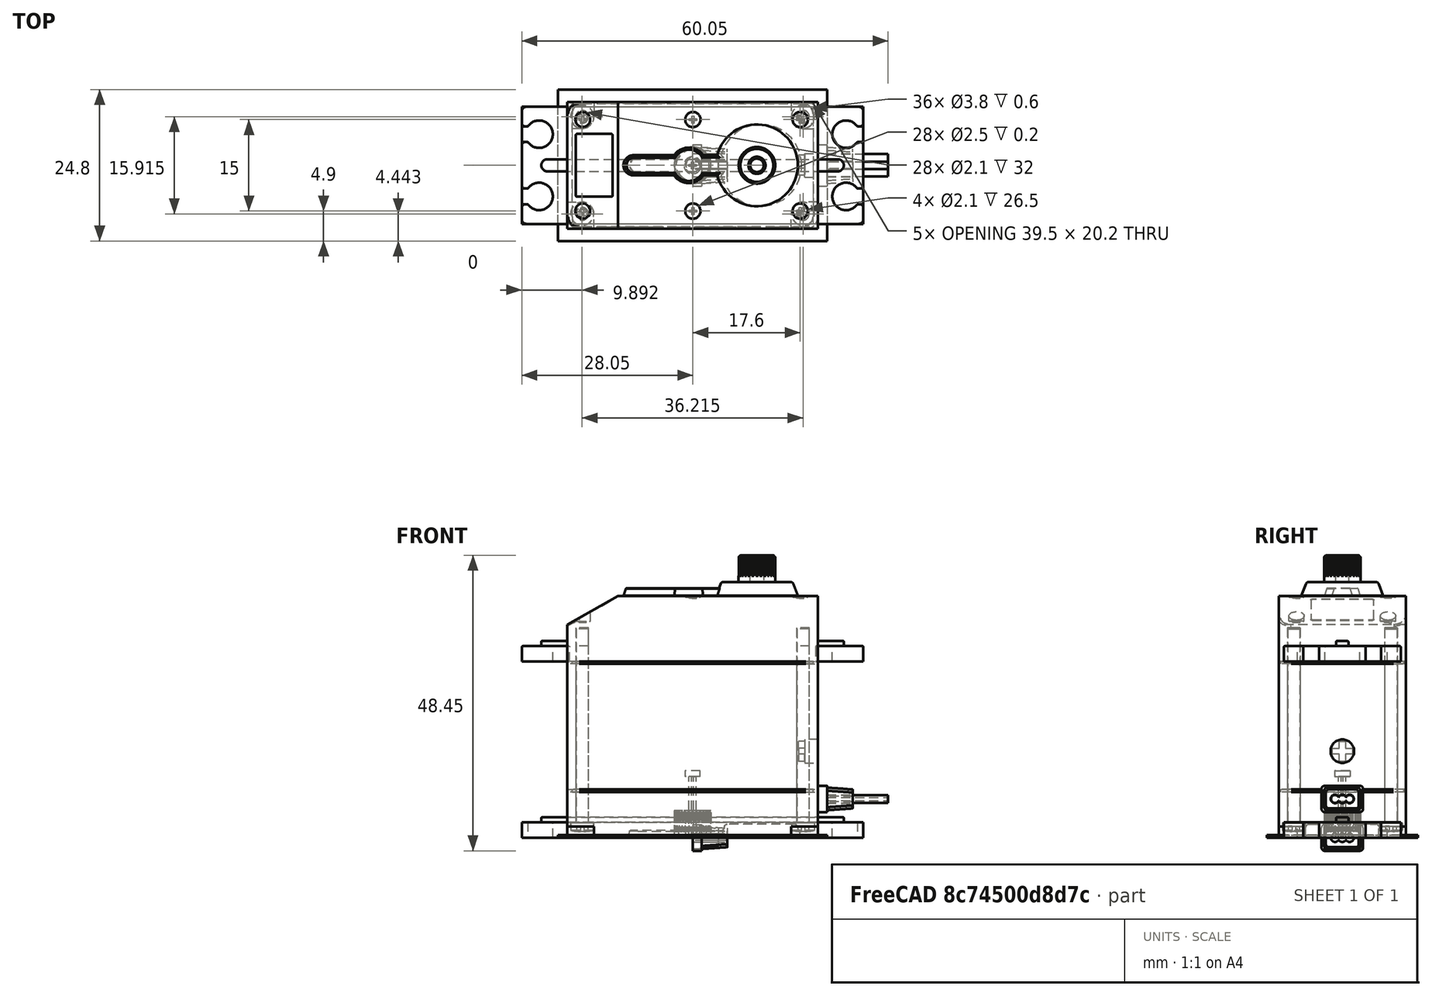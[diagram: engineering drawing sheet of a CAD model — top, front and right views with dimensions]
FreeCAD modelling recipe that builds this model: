
FCSTD DOCUMENT  (FreeCAD 0.19R24291 (Git))
Label: servo
License: CC-BY 3.0
LicenseURL: http://creativecommons.org/licenses/by/3.0/
objects: Sketcher::SketchObject×27, Part::Feature×24, PartDesign::Pocket×12, PartDesign::Pad×9, Part::Fillet×7, Part::MultiFuse×6, App::DocumentObjectGroup×5, Part::Compound×4, Part::Loft×3, PartDesign::Mirrored×2, Part::Cut×2, PartDesign::Fillet×2, PartDesign::Chamfer×2, PartDesign::PolarPattern×1, Part::Cylinder×1
note: 127 computed .brp shape members not serialized (recipe doc carries the construction recipe); baked Part::Feature solids carry a one-line shape summary decoded from their .brp

FEATURE [Sketcher::SketchObject] Sketch  label="servo-body-sketch"
  FullyConstrained = false
  MapMode = 5
  Placement = pos=(0,0,0) rot=(1,0,0;1.5708rad)
  sketch-geometry (5):
    g0: LineSegment StartX=20.55 StartY=39.6 StartZ=0 EndX=20.55 EndY=0 EndZ=0
    g1: LineSegment StartX=20.55 StartY=0 StartZ=0 EndX=-20.55 EndY=0 EndZ=0
    g2: LineSegment StartX=-20.55 StartY=0 StartZ=0 EndX=-20.55 EndY=34.9 EndZ=0
    g3: LineSegment StartX=-20.55 StartY=34.9 StartZ=0 EndX=-12.25 EndY=39.6 EndZ=0
    g4: LineSegment StartX=-12.25 StartY=39.6 StartZ=0 EndX=20.55 EndY=39.6 EndZ=0
  constraints (15):
    c: Coincident(g0,g1)
    c: Coincident(g1,g2)
    c: Horizontal(g1)
    c: Vertical(g0)
    c: Vertical(g2)
    c: Symmetric(g1,g0,g-2)
    c: PointOnObject(g1,g-1)
    c: DistanceX(g1) = -41.1
    c: DistanceY(g0) = -39.6
    c: Coincident(g3,g2)
    c: Horizontal(g4)
    c: Coincident(g4,g0)
    c: Coincident(g3,g4)
    c: DistanceY(g2) = 34.9
    c: DistanceX(g4) = 32.8
FEATURE [PartDesign::Pad] Pad  label="servo-body-1"
  AllowMultiFace = false
  Direction = (1,1,1)
  Length = 20.8
  Length2 = 100
  Midplane = true
  Placement = pos=(0,0,0) rot=(1,0,0;1.5708rad)
  Profile = -> Sketch
  Type = 0
FEATURE [Sketcher::SketchObject] Sketch001  label="bottom-master-sketch"
  ExternalGeometry = -> [Pad]
  FullyConstrained = false
  MapMode = 5
  Placement = pos=(0,0,0) rot=(1,0,0;3.14159rad)
  Support = -> [Pad]
  sketch-geometry (15):
    g0: LineSegment StartX=-20.55 StartY=10.4 StartZ=0 EndX=-18.2075 EndY=8.05754 EndZ=0
    g1: Circle CenterX=-18.2075 CenterY=8.05754 CenterZ=0 NormalX=0 NormalY=0 NormalZ=1 AngleXU=0 Radius=1.05
    g2: GeomPoint X=-18.95 Y=8.8 Z=0
    g3: LineSegment StartX=-18.2075 StartY=8.05754 StartZ=0 EndX=-18.2075 EndY=6 EndZ=0
    g4: LineSegment StartX=-18.2075 StartY=8.05754 StartZ=0 EndX=-16.15 EndY=8.05754 EndZ=0
    g5: LineSegment StartX=-20.55 StartY=6 StartZ=0 EndX=-20.55 EndY=10.4 EndZ=0
    g6: LineSegment StartX=-20.55 StartY=10.4 StartZ=0 EndX=-16.15 EndY=10.4 EndZ=0
    g7: LineSegment StartX=-16.15 StartY=10.4 StartZ=0 EndX=-16.15 EndY=8.05754 EndZ=0
    g8: ArcOfCircle CenterX=-18.2075 CenterY=8.05754 CenterZ=0 NormalX=0 NormalY=0 NormalZ=1 AngleXU=0 Radius=2.05754 StartAngle=4.71239 EndAngle=6.28319
    g9: LineSegment StartX=-20.55 StartY=6 StartZ=0 EndX=-18.2075 EndY=6 EndZ=0
    g10: ArcOfCircle CenterX=-18.2075 CenterY=-8.05754 CenterZ=0 NormalX=0 NormalY=0 NormalZ=1 AngleXU=0 Radius=2.05754 StartAngle=5.46325e-06 EndAngle=1.5708
    g11: LineSegment StartX=-18.2075 StartY=-6 StartZ=0 EndX=-20.55 EndY=-6 EndZ=0
    g12: LineSegment StartX=-20.55 StartY=-6 StartZ=0 EndX=-20.55 EndY=-10.4 EndZ=0
    g13: LineSegment StartX=-20.55 StartY=-10.4 StartZ=0 EndX=-16.15 EndY=-10.4 EndZ=0
    g14: LineSegment StartX=-16.15 StartY=-10.4 StartZ=0 EndX=-16.15 EndY=-8.05753 EndZ=0
  constraints (40):
    c: Coincident(g0,g-4)
    c: Angle(g-4,g0) = 0.785398
    c: Radius(g1) = 1.05
    c: Coincident(g1,g0)
    c: PointOnObject(g2,g0)
    c: PointOnObject(g2,g1)
    c: DistanceX(g2,g0) = -1.6
    c: Vertical(g3)
    c: Coincident(g3,g0)
    c: Coincident(g0,g4)
    c: Horizontal(g4)
    c: Equal(g3,g4)
    c: Coincident(g5,g6)
    c: Vertical(g5)
    c: Horizontal(g6)
    c: Vertical(g7)
    c: Coincident(g7,g6)
    c: Coincident(g7,g4)
    c: Coincident(g5,g0)
    c: Coincident(g8,g0)
    c: Coincident(g8,g4)
    c: Coincident(g3,g8)
    c: Coincident(g9,g5)
    c: Coincident(g9,g3)
    c: Horizontal(g9)
    c: DistanceY(g0,g5) = -4.4
    c: Horizontal(g11)
    c: Coincident(g11,g12)
    c: Vertical(g12)
    c: Coincident(g12,g13)
    c: Horizontal(g13)
    c: Coincident(g13,g14)
    c: Vertical(g14)
    c: Coincident(g12,g-4)
    c: Symmetric(g10,g0,g-1)
    c: Symmetric(g13,g6,g-1)
    c: Symmetric(g11,g3,g-1)
    c: Equal(g10,g8)
    c: Coincident(g10,g11)
    c: Coincident(g10,g14)
FEATURE [PartDesign::Pocket] Pocket  label="bottom-master"
  AllowMultiFace = false
  Length = 1.8
  Length2 = 100
  Placement = pos=(0,0,0) rot=(1,0,0;1.5708rad)
  Profile = -> Sketch001
  Type = 0
FEATURE [PartDesign::Mirrored] Mirrored  label="bottom-1"
  MirrorPlane = -> Sketch001 [V_Axis]
  Originals = -> [Pocket]
  Placement = pos=(0,0,0) rot=(1,0,0;1.5708rad)
FEATURE [Sketcher::SketchObject] Sketch002  label="bottom-2-sketch"
  ExternalGeometry = -> [Mirrored]
  FullyConstrained = false
  MapMode = 5
  Placement = pos=(0,1e-15,1.8) rot=(1,0,0;3.14159rad)
  Support = -> [Mirrored]
  sketch-geometry (10):
    g0: LineSegment StartX=-20.55 StartY=10.4 StartZ=0 EndX=-18.85 EndY=8.7 EndZ=0
    g1: Circle CenterX=-18.1075 CenterY=7.95754 CenterZ=0 NormalX=0 NormalY=0 NormalZ=1 AngleXU=0 Radius=1.05
    g2: Circle CenterX=-18.1075 CenterY=7.95754 CenterZ=0 NormalX=0 NormalY=0 NormalZ=1 AngleXU=0 Radius=1.9
    g3: Circle CenterX=-18.1075 CenterY=-7.95754 CenterZ=0 NormalX=0 NormalY=0 NormalZ=1 AngleXU=0 Radius=1.9
    g4: Circle CenterX=18.1075 CenterY=7.95754 CenterZ=0 NormalX=0 NormalY=0 NormalZ=1 AngleXU=0 Radius=1.9
    g5: Circle CenterX=18.1075 CenterY=-7.95754 CenterZ=0 NormalX=0 NormalY=0 NormalZ=1 AngleXU=0 Radius=1.9
    g6: LineSegment StartX=-18.1075 StartY=7.95754 StartZ=0 EndX=18.1075 EndY=7.95754 EndZ=0
    g7: LineSegment StartX=18.1075 StartY=7.95754 StartZ=0 EndX=18.1075 EndY=-7.95754 EndZ=0
    g8: LineSegment StartX=18.1075 StartY=-7.95754 StartZ=0 EndX=-18.1075 EndY=-7.95754 EndZ=0
    g9: LineSegment StartX=-18.1075 StartY=-7.95754 StartZ=0 EndX=-18.1075 EndY=7.95754 EndZ=0
  constraints (24):
    c: Angle(g0,g-3) = 0.785398
    c: Coincident(g0,g-3)
    c: Radius(g1) = 1.05
    c: PointOnObject(g1,g0)
    c: PointOnObject(g0,g1)
    c: DistanceX(g0,g0) = 1.7
    c: Coincident(g2,g1)
    c: Radius(g2) = 1.9
    c: Equal(g3,g2)
    c: Equal(g2,g4)
    c: Equal(g4,g5)
    c: Coincident(g6,g7)
    c: Coincident(g7,g8)
    c: Coincident(g8,g9)
    c: Coincident(g9,g6)
    c: Horizontal(g6)
    c: Horizontal(g8)
    c: Vertical(g7)
    c: Vertical(g9)
    c: Symmetric(g6,g7,g-1)
    c: Coincident(g6,g1)
    c: Coincident(g3,g8)
    c: Coincident(g6,g4)
    c: Coincident(g5,g7)
FEATURE [PartDesign::Pocket] Pocket001  label="bottom-2"
  AllowMultiFace = false
  Length = 0.6
  Length2 = 100
  Placement = pos=(0,0,0) rot=(1,0,0;1.5708rad)
  Profile = -> Sketch002
  Type = 0
FEATURE [Sketcher::SketchObject] Sketch003  label="bottom-drills-sketch"
  ExternalGeometry = -> [Pocket001]
  FullyConstrained = false
  MapMode = 5
  Placement = pos=(0,1.6e-15,2.4) rot=(1,0,0;3.14159rad)
  Support = -> [Pocket001]
  sketch-geometry (8):
    g0: Circle CenterX=-18.1075 CenterY=7.95754 CenterZ=0 NormalX=0 NormalY=0 NormalZ=1 AngleXU=0 Radius=1.05
    g1: LineSegment StartX=-18.1075 StartY=7.95754 StartZ=0 EndX=18.1075 EndY=7.95754 EndZ=0
    g2: LineSegment StartX=18.1075 StartY=7.95754 StartZ=0 EndX=18.1075 EndY=-7.95754 EndZ=0
    g3: LineSegment StartX=18.1075 StartY=-7.95754 StartZ=0 EndX=-18.1075 EndY=-7.95754 EndZ=0
    g4: LineSegment StartX=-18.1075 StartY=-7.95754 StartZ=0 EndX=-18.1075 EndY=7.95754 EndZ=0
    g5: Circle CenterX=-18.1075 CenterY=-7.95754 CenterZ=0 NormalX=0 NormalY=0 NormalZ=1 AngleXU=0 Radius=1.05
    g6: Circle CenterX=18.1075 CenterY=7.95754 CenterZ=0 NormalX=0 NormalY=0 NormalZ=1 AngleXU=0 Radius=1.05
    g7: Circle CenterX=18.1075 CenterY=-7.95754 CenterZ=0 NormalX=0 NormalY=0 NormalZ=1 AngleXU=0 Radius=1.05
  constraints (18):
    c: Coincident(g0,g-3)
    c: Radius(g0) = 1.05
    c: Coincident(g1,g2)
    c: Coincident(g2,g3)
    c: Coincident(g3,g4)
    c: Coincident(g4,g1)
    c: Horizontal(g1)
    c: Horizontal(g3)
    c: Vertical(g2)
    c: Vertical(g4)
    c: Symmetric(g1,g2,g-1)
    c: Coincident(g1,g0)
    c: Equal(g6,g5)
    c: Equal(g5,g7)
    c: Equal(g7,g0)
    c: Coincident(g3,g5)
    c: Coincident(g6,g1)
    c: Coincident(g7,g2)
FEATURE [PartDesign::Pocket] Pocket002  label="bottom-drills"
  AllowMultiFace = false
  Length = 32
  Length2 = 100
  Placement = pos=(0,0,0) rot=(1,0,0;1.5708rad)
  Profile = -> Sketch003
  Type = 0
FEATURE [Sketcher::SketchObject] Sketch004  label="top-drills-1-sketch"
  ExternalGeometry = -> [Pocket002]
  FullyConstrained = false
  MapMode = 5
  Placement = pos=(0,3.08e-14,39.6) rot=(0,0,1;3.14159rad)
  Support = -> [Pocket002]
  sketch-geometry (9):
    g0: LineSegment StartX=-17.65 StartY=7.5 StartZ=0 EndX=-0.05 EndY=7.5 EndZ=0
    g1: LineSegment StartX=-0.05 StartY=7.5 StartZ=0 EndX=-0.05 EndY=-7.5 EndZ=0
    g2: LineSegment StartX=-0.05 StartY=-7.5 StartZ=0 EndX=-17.65 EndY=-7.5 EndZ=0
    g3: LineSegment StartX=-17.65 StartY=-7.5 StartZ=0 EndX=-17.65 EndY=7.5 EndZ=0
    g4: Circle CenterX=-0.05 CenterY=-7.5 CenterZ=0 NormalX=0 NormalY=0 NormalZ=1 AngleXU=0 Radius=1.25
    g5: Circle CenterX=-17.65 CenterY=-7.5 CenterZ=0 NormalX=0 NormalY=0 NormalZ=1 AngleXU=0 Radius=1.25
    g6: Circle CenterX=-0.05 CenterY=7.5 CenterZ=0 NormalX=0 NormalY=0 NormalZ=1 AngleXU=0 Radius=1.25
    g7: Circle CenterX=-17.65 CenterY=7.5 CenterZ=0 NormalX=0 NormalY=0 NormalZ=1 AngleXU=0 Radius=1.25
    g8: LineSegment StartX=-20.55 StartY=-10.4 StartZ=0 EndX=-17.65 EndY=-7.5 EndZ=0
  constraints (22):
    c: Coincident(g0,g1)
    c: Coincident(g1,g2)
    c: Coincident(g2,g3)
    c: Coincident(g3,g0)
    c: Horizontal(g0)
    c: Horizontal(g2)
    c: Vertical(g1)
    c: Vertical(g3)
    c: Symmetric(g2,g0,g-1)
    c: Equal(g4,g7)
    c: Equal(g7,g6)
    c: Equal(g6,g5)
    c: Radius(g4) = 1.25
    c: Coincident(g4,g1)
    c: Coincident(g6,g0)
    c: Coincident(g5,g2)
    c: Coincident(g7,g0)
    c: DistanceY(g-1,g1) = -7.5
    c: DistanceX(g2) = -17.6
    c: Coincident(g8,g-3)
    c: Coincident(g8,g2)
    c: Angle(g-3,g8) = 0.785398
FEATURE [PartDesign::Pocket] Pocket003  label="top-drills-1"
  AllowMultiFace = false
  Length = 0.2
  Length2 = 100
  Placement = pos=(0,0,0) rot=(1,0,0;1.5708rad)
  Profile = -> Sketch004
  Type = 0
FEATURE [Sketcher::SketchObject] Sketch006  label="potentiometer-1-sketch"
  FullyConstrained = false
  MapMode = 5
  Placement = pos=(20.55,0,0) rot=(0.707107,0,0.707107;3.14159rad)
  Support = -> [Pocket003]
  sketch-geometry (2):
    g0: Circle CenterX=14.175 CenterY=0 CenterZ=0 NormalX=0 NormalY=0 NormalZ=1 AngleXU=0 Radius=1.925
    g1: GeomPoint X=16.1 Y=0 Z=0
  constraints (5):
    c: PointOnObject(g0,g-1)
    c: Radius(g0) = 1.925
    c: PointOnObject(g1,g-1)
    c: PointOnObject(g1,g0)
    c: DistanceX(g-1,g1) = 16.1
FEATURE [PartDesign::Pocket] Pocket004  label="potentiometer-hole"
  AllowMultiFace = false
  Length = 2.2
  Length2 = 100
  Placement = pos=(0,0,0) rot=(1,0,0;1.5708rad)
  Profile = -> Sketch006
  Type = 0
FEATURE [Sketcher::SketchObject] Sketch007  label="potentiometer-cross-sketch"
  ExternalGeometry = -> [Pocket004]
  FullyConstrained = false
  MapMode = 5
  Placement = pos=(18.35,0,0) rot=(0.707107,0,0.707107;3.14159rad)
  Support = -> [Pocket004]
  sketch-geometry (12):
    g0: LineSegment StartX=13.675 StartY=1.65 StartZ=0 EndX=14.675 EndY=1.65 EndZ=0
    g1: LineSegment StartX=14.675 StartY=1.65 StartZ=0 EndX=14.675 EndY=0.5 EndZ=0
    g2: LineSegment StartX=14.675 StartY=-1.65 StartZ=0 EndX=13.675 EndY=-1.65 EndZ=0
    g3: LineSegment StartX=13.675 StartY=-1.65 StartZ=0 EndX=13.675 EndY=-0.5 EndZ=0
    g4: LineSegment StartX=12.525 StartY=0.5 StartZ=0 EndX=13.675 EndY=0.5 EndZ=0
    g5: LineSegment StartX=15.825 StartY=0.5 StartZ=0 EndX=15.825 EndY=-0.5 EndZ=0
    g6: LineSegment StartX=15.825 StartY=-0.5 StartZ=0 EndX=14.675 EndY=-0.5 EndZ=0
    g7: LineSegment StartX=12.525 StartY=-0.5 StartZ=0 EndX=12.525 EndY=0.5 EndZ=0
    g8: LineSegment StartX=14.675 StartY=0.5 StartZ=0 EndX=15.825 EndY=0.5 EndZ=0
    g9: LineSegment StartX=13.675 StartY=-0.5 StartZ=0 EndX=12.525 EndY=-0.5 EndZ=0
    g10: LineSegment StartX=13.675 StartY=0.5 StartZ=0 EndX=13.675 EndY=1.65 EndZ=0
    g11: LineSegment StartX=14.675 StartY=-0.5 StartZ=0 EndX=14.675 EndY=-1.65 EndZ=0
  constraints (30):
    c: Coincident(g0,g1)
    c: Coincident(g11,g2)
    c: Coincident(g2,g3)
    c: Coincident(g10,g0)
    c: Horizontal(g0)
    c: Horizontal(g2)
    c: Vertical(g1)
    c: Vertical(g3)
    c: Coincident(g8,g5)
    c: Coincident(g5,g6)
    c: Coincident(g9,g7)
    c: Coincident(g7,g4)
    c: Horizontal(g4)
    c: Horizontal(g6)
    c: Vertical(g5)
    c: Vertical(g7)
    c: Symmetric(g4,g5,g-3)
    c: Symmetric(g0,g11,g-3)
    c: Tangent(g4,g8)
    c: Tangent(g6,g9)
    c: Coincident(g3,g9)
    c: Coincident(g10,g4)
    c: Tangent(g3,g10)
    c: Coincident(g1,g8)
    c: Coincident(g11,g6)
    c: Tangent(g1,g11)
    c: Equal(g4,g10)
    c: Equal(g7,g0)
    c: DistanceX(g5,g4) = -3.3
    c: DistanceY(g5) = -1
FEATURE [PartDesign::Pocket] Pocket005  label="potentiometer-cross"
  AllowMultiFace = false
  Length = 1
  Length2 = 100
  Placement = pos=(0,0,0) rot=(1,0,0;1.5708rad)
  Profile = -> Sketch007
  Type = 0
FEATURE [Sketcher::SketchObject] Sketch008  label="label-plate-sketch"
  ExternalGeometry = -> [Pocket005]
  FullyConstrained = false
  MapMode = 5
  Placement = pos=(-19.9538,7.43e-14,35.2376) rot=(-0.254782,0,0.966998;3.14159rad)
  Support = -> [Pocket005]
  sketch-geometry (8):
    g0: LineSegment StartX=-7.65321 StartY=5.15 StartZ=0 EndX=-1.15321 EndY=5.15 EndZ=0
    g1: LineSegment StartX=-0.953214 StartY=4.95 StartZ=0 EndX=-0.953214 EndY=-4.95 EndZ=0
    g2: LineSegment StartX=-1.15321 StartY=-5.15 StartZ=0 EndX=-7.65321 EndY=-5.15 EndZ=0
    g3: LineSegment StartX=-7.85321 StartY=-4.95 StartZ=0 EndX=-7.85321 EndY=4.95 EndZ=0
    g4: ArcOfCircle CenterX=-7.65321 CenterY=4.95 CenterZ=0 NormalX=0 NormalY=0 NormalZ=1 AngleXU=0 Radius=0.2 StartAngle=1.5708 EndAngle=3.14159
    g5: ArcOfCircle CenterX=-1.15321 CenterY=4.95 CenterZ=0 NormalX=0 NormalY=0 NormalZ=1 AngleXU=0 Radius=0.2 StartAngle=0 EndAngle=1.5708
    g6: ArcOfCircle CenterX=-1.15321 CenterY=-4.95 CenterZ=0 NormalX=0 NormalY=0 NormalZ=1 AngleXU=0 Radius=0.2 StartAngle=4.71239 EndAngle=6.28319
    g7: ArcOfCircle CenterX=-7.65321 CenterY=-4.95 CenterZ=0 NormalX=0 NormalY=0 NormalZ=1 AngleXU=0 Radius=0.2 StartAngle=3.14159 EndAngle=4.71239
  constraints (20):
    c: Horizontal(g0)
    c: Horizontal(g2)
    c: Vertical(g1)
    c: Vertical(g3)
    c: Tangent(g0,g4)
    c: Tangent(g3,g4)
    c: Tangent(g0,g5)
    c: Tangent(g1,g5)
    c: Tangent(g1,g6)
    c: Tangent(g2,g6)
    c: Tangent(g2,g7)
    c: Tangent(g3,g7)
    c: Equal(g4,g5)
    c: Equal(g5,g7)
    c: Equal(g7,g6)
    c: Symmetric(g5,g6,g-1)
    c: DistanceY(g0,g2) = -10.3
    c: DistanceX(g3,g1) = 6.9
    c: Radius(g4) = 0.2
    c: DistanceX(g3,g-3) = -1
FEATURE [PartDesign::Pocket] Pocket006  label="Label-plate"
  AllowMultiFace = false
  Length = 0.1
  Length2 = 100
  Placement = pos=(0,0,0) rot=(1,0,0;1.5708rad)
  Profile = -> Sketch008
  Type = 0
FEATURE [Sketcher::SketchObject] Sketch009  label="top-left-2-drills-sketch"
  FullyConstrained = false
  MapMode = 5
  Placement = pos=(0,1.011e-13,39.6) rot=(0,0,1;3.14159rad)
  Support = -> [Pocket006]
  sketch-geometry (4):
    g0: Circle CenterX=18 CenterY=7.5 CenterZ=0 NormalX=0 NormalY=0 NormalZ=1 AngleXU=0 Radius=1.25
    g1: Circle CenterX=18 CenterY=-7.5 CenterZ=0 NormalX=0 NormalY=0 NormalZ=1 AngleXU=0 Radius=1.25
    g2: LineSegment StartX=18 StartY=7.5 StartZ=0 EndX=18 EndY=0 EndZ=0
    g3: LineSegment StartX=18 StartY=7.5 StartZ=0 EndX=19.25 EndY=7.5 EndZ=0
  constraints (10):
    c: Radius(g0) = 1.25
    c: Equal(g1,g0)
    c: Symmetric(g0,g1,g-1)
    c: Coincident(g2,g0)
    c: Vertical(g2)
    c: PointOnObject(g2,g-1)
    c: DistanceY(g2) = -7.5
    c: Horizontal(g3)
    c: Coincident(g3,g0)
    c: PointOnObject(g3,g0)
FEATURE [PartDesign::Pocket] Pocket007  label="top-left-2-drills"
  AllowMultiFace = false
  Length = 4.1
  Length2 = 100
  Placement = pos=(0,0,0) rot=(1,0,0;1.5708rad)
  Profile = -> Sketch009
  Type = 0
FEATURE [Sketcher::SketchObject] Sketch010  label="top-drills-cross-1-sketch"
  FullyConstrained = false
  MapMode = 5
  sketch-geometry (13):
    g0: Circle CenterX=0 CenterY=0 CenterZ=0 NormalX=0 NormalY=0 NormalZ=1 AngleXU=0 Radius=1.25
    g1: LineSegment StartX=-0.15 StartY=0.6 StartZ=0 EndX=0.15 EndY=0.6 EndZ=0
    g2: LineSegment StartX=0.15 StartY=0.6 StartZ=0 EndX=0.15 EndY=0.15 EndZ=0
    g3: LineSegment StartX=0.15 StartY=-0.6 StartZ=0 EndX=-0.15 EndY=-0.6 EndZ=0
    g4: LineSegment StartX=-0.15 StartY=-0.6 StartZ=0 EndX=-0.15 EndY=-0.15 EndZ=0
    g5: LineSegment StartX=-0.6 StartY=0.15 StartZ=0 EndX=-0.15 EndY=0.15 EndZ=0
    g6: LineSegment StartX=0.6 StartY=0.15 StartZ=0 EndX=0.6 EndY=-0.15 EndZ=0
    g7: LineSegment StartX=0.6 StartY=-0.15 StartZ=0 EndX=0.15 EndY=-0.15 EndZ=0
    g8: LineSegment StartX=-0.6 StartY=-0.15 StartZ=0 EndX=-0.6 EndY=0.15 EndZ=0
    g9: LineSegment StartX=0.15 StartY=0.15 StartZ=0 EndX=0.6 EndY=0.15 EndZ=0
    g10: LineSegment StartX=-0.15 StartY=-0.15 StartZ=0 EndX=-0.6 EndY=-0.15 EndZ=0
    g11: LineSegment StartX=-0.15 StartY=0.15 StartZ=0 EndX=-0.15 EndY=0.6 EndZ=0
    g12: LineSegment StartX=0.15 StartY=-0.15 StartZ=0 EndX=0.15 EndY=-0.6 EndZ=0
  constraints (32):
    c: Coincident(g0,g-1)
    c: Radius(g0) = 1.25
    c: Coincident(g1,g2)
    c: Coincident(g12,g3)
    c: Coincident(g3,g4)
    c: Coincident(g11,g1)
    c: Horizontal(g1)
    c: Horizontal(g3)
    c: Vertical(g2)
    c: Vertical(g4)
    c: Symmetric(g1,g12,g-1)
    c: Coincident(g9,g6)
    c: Coincident(g6,g7)
    c: Coincident(g10,g8)
    c: Coincident(g8,g5)
    c: Horizontal(g5)
    c: Horizontal(g7)
    c: Vertical(g6)
    c: Vertical(g8)
    c: Symmetric(g5,g6,g-1)
    c: Tangent(g5,g9)
    c: Tangent(g7,g10)
    c: Coincident(g4,g10)
    c: Coincident(g11,g5)
    c: Tangent(g4,g11)
    c: Coincident(g2,g9)
    c: Coincident(g12,g7)
    c: Tangent(g2,g12)
    c: Equal(g5,g11)
    c: Equal(g8,g1)
    c: DistanceX(g5,g6) = 1.2
    c: DistanceX(g1) = 0.3
FEATURE [PartDesign::Pad] Pad001  label="top-drills-cross-1"
  AllowMultiFace = false
  Direction = (1,1,1)
  Length = 10
  Length2 = 100
  Profile = -> Sketch010
  Type = 0
FEATURE [Sketcher::SketchObject] Sketch011  label="top-drills-cross-2-sketch"
  FullyConstrained = false
  MapMode = 5
  Placement = pos=(0,0,10) rot=(0,0,1;0rad)
  Support = -> [Pad001]
  sketch-geometry (1):
    g0: Circle CenterX=0 CenterY=0 CenterZ=0 NormalX=0 NormalY=0 NormalZ=1 AngleXU=0 Radius=1.25
  constraints (2):
    c: Coincident(g0,g-1)
    c: Radius(g0) = 1.25
FEATURE [PartDesign::Pad] Pad002  label="top-drills-cross-2"
  AllowMultiFace = false
  Direction = (1,1,1)
  Length = 1
  Length2 = 100
  Profile = -> Sketch011
  Type = 0
FEATURE [Part::Feature] Pad002001  label="top-drills-cross-01"
  Placement = pos=(17.65,7.5,39.2) rot=(0,0,1;0rad)
  shape: bbox 2.5 x 2.5 x 11 mm, 16 faces (baked)
FEATURE [Part::Feature] Pad002001001  label="top-drills-cross-002"
  Placement = pos=(17.65,-7.5,39.2) rot=(0,0,1;0rad)
  shape: bbox 2.5 x 2.5 x 11 mm, 16 faces (baked)
FEATURE [Part::Feature] Pad002001002  label="top-drills-cross-003"
  Placement = pos=(0.05,7.5,39.2) rot=(0,0,1;0rad)
  shape: bbox 2.5 x 2.5 x 11 mm, 16 faces (baked)
FEATURE [Part::Feature] Pad002001003  label="top-drills-cross-004"
  Placement = pos=(0.05,-7.5,39.2) rot=(0,0,1;0rad)
  shape: bbox 2.5 x 2.5 x 11 mm, 16 faces (baked)
FEATURE [Part::Feature] Pad002001003001  label="top-drills-cross-005"
  Placement = pos=(-18,7.5,35.2) rot=(0,0,1;0rad)
  shape: bbox 2.5 x 2.5 x 11 mm, 16 faces (baked)
FEATURE [Part::Feature] Pad002001003002  label="top-drills-cross-006"
  Placement = pos=(-18,-7.5,35.2) rot=(0,0,1;0rad)
  shape: bbox 2.5 x 2.5 x 11 mm, 16 faces (baked)
FEATURE [Part::MultiFuse] Fusion  label="union-of-top-crosses"
  Shapes = -> [Pad002001,Pad002001003001,Pad002001003002,Pad002001002,Pad002001003,Pad002001001]
FEATURE [Part::Cut] Cut  label="servo-body-final-1"
  Base = -> Pocket007
  Tool = -> Fusion
FEATURE [Sketcher::SketchObject] Sketch012  label="shaft-anchor-sketch"
  ExternalGeometry = -> [Cut]
  FullyConstrained = false
  MapMode = 5
  Placement = pos=(0,1.187e-13,39.6) rot=(0,0,1;0rad)
  Support = -> [Cut]
  sketch-geometry (2):
    g0: Circle CenterX=10.55 CenterY=0 CenterZ=0 NormalX=0 NormalY=0 NormalZ=1 AngleXU=0 Radius=3
    g1: LineSegment StartX=13.55 StartY=0 StartZ=0 EndX=20.55 EndY=0 EndZ=0
  constraints (7):
    c: PointOnObject(g0,g-1)
    c: Radius(g0) = 3
    c: Horizontal(g1)
    c: PointOnObject(g1,g-3)
    c: PointOnObject(g1,g-1)
    c: PointOnObject(g1,g0)
    c: DistanceX(g1) = 7
FEATURE [PartDesign::Pad] Pad002001003003  label="servo-body-final-2"
  AllowMultiFace = false
  Direction = (1,1,1)
  Length = 0.1
  Length2 = 100
  Profile = -> Sketch012
  Type = 0
FEATURE [Sketcher::SketchObject] Sketch013  label="side-gap-sketch"
  FullyConstrained = false
  MapMode = 5
  sketch-geometry (25):
    g0: LineSegment StartX=-18.05 StartY=10.4 StartZ=0 EndX=18.05 EndY=10.4 EndZ=0
    g1: LineSegment StartX=20.05 StartY=8.4 StartZ=0 EndX=20.05 EndY=-8.4 EndZ=0
    g2: LineSegment StartX=18.05 StartY=-10.4 StartZ=0 EndX=-18.05 EndY=-10.4 EndZ=0
    g3: LineSegment StartX=-20.05 StartY=-8.4 StartZ=0 EndX=-20.05 EndY=8.4 EndZ=0
    g4: LineSegment StartX=-22.05 StartY=12.4 StartZ=0 EndX=-18.05 EndY=8.4 EndZ=0
    g5: LineSegment StartX=-18.05 StartY=10.1 StartZ=0 EndX=18.05 EndY=10.1 EndZ=0
    g6: LineSegment StartX=19.75 StartY=8.4 StartZ=0 EndX=19.75 EndY=-8.4 EndZ=0
    g7: LineSegment StartX=18.05 StartY=-10.1 StartZ=0 EndX=-18.05 EndY=-10.1 EndZ=0
    g8: LineSegment StartX=-19.75 StartY=-8.4 StartZ=0 EndX=-19.75 EndY=8.4 EndZ=0
    g9: LineSegment StartX=-22.05 StartY=12.4 StartZ=0 EndX=22.05 EndY=12.4 EndZ=0
    g10: LineSegment StartX=22.05 StartY=12.4 StartZ=0 EndX=22.05 EndY=-12.4 EndZ=0
    g11: LineSegment StartX=22.05 StartY=-12.4 StartZ=0 EndX=-22.05 EndY=-12.4 EndZ=0
    g12: LineSegment StartX=-22.05 StartY=-12.4 StartZ=0 EndX=-22.05 EndY=12.4 EndZ=0
    g13: ArcOfCircle CenterX=18.05 CenterY=-8.4 CenterZ=0 NormalX=0 NormalY=0 NormalZ=1 AngleXU=0 Radius=2 StartAngle=4.71239 EndAngle=6.28319
    g14: ArcOfCircle CenterX=18.05 CenterY=8.4 CenterZ=0 NormalX=0 NormalY=0 NormalZ=1 AngleXU=0 Radius=2 StartAngle=0 EndAngle=1.5708
    g15: ArcOfCircle CenterX=-18.05 CenterY=8.4 CenterZ=0 NormalX=0 NormalY=0 NormalZ=1 AngleXU=0 Radius=2 StartAngle=1.5708 EndAngle=3.14159
    g16: ArcOfCircle CenterX=-18.05 CenterY=-8.4 CenterZ=0 NormalX=0 NormalY=0 NormalZ=1 AngleXU=0 Radius=2 StartAngle=3.14159 EndAngle=4.71239
    g17: LineSegment StartX=-18.05 StartY=8.4 StartZ=0 EndX=18.05 EndY=8.4 EndZ=0
    g18: LineSegment StartX=18.05 StartY=8.4 StartZ=0 EndX=18.05 EndY=-8.4 EndZ=0
    g19: LineSegment StartX=18.05 StartY=-8.4 StartZ=0 EndX=-18.05 EndY=-8.4 EndZ=0
    g20: LineSegment StartX=-18.05 StartY=-8.4 StartZ=0 EndX=-18.05 EndY=8.4 EndZ=0
    g21: ArcOfCircle CenterX=-18.05 CenterY=8.4 CenterZ=0 NormalX=0 NormalY=0 NormalZ=1 AngleXU=0 Radius=1.7 StartAngle=1.5708 EndAngle=3.14159
    g22: ArcOfCircle CenterX=-18.05 CenterY=-8.4 CenterZ=0 NormalX=0 NormalY=0 NormalZ=1 AngleXU=0 Radius=1.7 StartAngle=3.14159 EndAngle=4.71239
    g23: ArcOfCircle CenterX=18.05 CenterY=-8.4 CenterZ=0 NormalX=0 NormalY=0 NormalZ=1 AngleXU=0 Radius=1.7 StartAngle=4.71239 EndAngle=6.28319
    g24: ArcOfCircle CenterX=18.05 CenterY=8.4 CenterZ=0 NormalX=0 NormalY=0 NormalZ=1 AngleXU=0 Radius=1.7 StartAngle=0 EndAngle=1.5708
  constraints (62):
    c: Horizontal(g0)
    c: Horizontal(g2)
    c: Vertical(g1)
    c: Vertical(g3)
    c: Angle(g-1,g4) = 2.35619
    c: Horizontal(g5)
    c: Horizontal(g7)
    c: Vertical(g6)
    c: Vertical(g8)
    c: Coincident(g9,g10)
    c: Coincident(g10,g11)
    c: Coincident(g11,g12)
    c: Coincident(g12,g9)
    c: Horizontal(g9)
    c: Horizontal(g11)
    c: Vertical(g10)
    c: Vertical(g12)
    c: PointOnObject(g9,g4)
    c: Symmetric(g9,g10,g-1)
    c: Coincident(g4,g9)
    c: Tangent(g1,g13)
    c: Tangent(g2,g13)
    c: Radius(g13) = 2
    c: Tangent(g0,g14)
    c: Tangent(g1,g14)
    c: Tangent(g0,g15)
    c: Tangent(g3,g15)
    c: Tangent(g2,g16)
    c: Tangent(g3,g16)
    c: Coincident(g17,g18)
    c: Coincident(g18,g19)
    c: Coincident(g19,g20)
    c: Coincident(g20,g17)
    c: Horizontal(g17)
    c: Horizontal(g19)
    c: Vertical(g18)
    c: Vertical(g20)
    c: Coincident(g17,g15)
    c: Symmetric(g15,g18,g-1)
    c: PointOnObject(g15,g4)
    c: Equal(g15,g16)
    c: Equal(g16,g14)
    c: Equal(g14,g13)
    c: DistanceX(g3,g1) = 40.1
    c: DistanceY(g0,g2) = -20.8
    c: Tangent(g8,g21)
    c: Tangent(g5,g21)
    c: PointOnObject(g21,g4)
    c: Coincident(g21,g15)
    c: Coincident(g4,g15)
    c: DistanceX(g8,g3) = -0.3
    c: DistanceX(g3,g4) = -2
    c: Tangent(g8,g22)
    c: Tangent(g7,g22)
    c: Coincident(g22,g16)
    c: Tangent(g7,g23)
    c: Tangent(g6,g23)
    c: Coincident(g23,g18)
    c: Tangent(g5,g24)
    c: Tangent(g6,g24)
    c: Coincident(g24,g17)
    c: Coincident(g14,g17)
FEATURE [PartDesign::Pad] Pad002001003004  label="side-gap-master"
  AllowMultiFace = false
  Direction = (1,1,1)
  Length = 0.4
  Length2 = 100
  Profile = -> Sketch013
  Type = 0
FEATURE [Sketcher::SketchObject] Sketch014  label="servo-top-1-sketch"
  FullyConstrained = false
  MapMode = 5
  sketch-geometry (10):
    g0: LineSegment StartX=-9.03485 StartY=1.65 StartZ=0 EndX=-9.03485 EndY=-1.65 EndZ=0
    g1: ArcOfCircle CenterX=-9.03485 CenterY=0 CenterZ=0 NormalX=0 NormalY=0 NormalZ=1 AngleXU=0 Radius=1.65 StartAngle=1.5708 EndAngle=4.71239
    g2: LineSegment StartX=-9.03485 StartY=1.65 StartZ=0 EndX=-2.38485 EndY=1.65 EndZ=0
    g3: LineSegment StartX=-9.03485 StartY=-1.65 StartZ=0 EndX=-2.38485 EndY=-1.65 EndZ=0
    g4: LineSegment StartX=11.1848 StartY=1.65 StartZ=0 EndX=11.1848 EndY=-1.65 EndZ=0
    g5: ArcOfCircle CenterX=0 CenterY=0 CenterZ=0 NormalX=0 NormalY=0 NormalZ=1 AngleXU=0 Radius=2.9 StartAngle=3.74684 EndAngle=5.67794
    g6: LineSegment StartX=2.38485 StartY=1.65 StartZ=0 EndX=11.1848 EndY=1.65 EndZ=0
    g7: ArcOfCircle CenterX=0 CenterY=0 CenterZ=0 NormalX=0 NormalY=0 NormalZ=1 AngleXU=0 Radius=2.9 StartAngle=0.605247 EndAngle=2.53635
    g8: LineSegment StartX=2.38485 StartY=-1.65 StartZ=0 EndX=11.1848 EndY=-1.65 EndZ=0
    g9: Circle CenterX=11.1848 CenterY=0 CenterZ=0 NormalX=0 NormalY=0 NormalZ=1 AngleXU=0 Radius=6.7
  constraints (29):
    c: Vertical(g0)
    c: Symmetric(g0,g0,g-1)
    c: Coincident(g1,g0)
    c: Coincident(g0,g1)
    c: PointOnObject(g1,g0)
    c: Horizontal(g2)
    c: Coincident(g2,g0)
    c: Horizontal(g3)
    c: Coincident(g3,g0)
    c: Coincident(g6,g4)
    c: Vertical(g4)
    c: Coincident(g4,g8)
    c: Tangent(g2,g6)
    c: PointOnObject(g7,g2)
    c: Equal(g5,g7)
    c: Coincident(g7,g6)
    c: Coincident(g5,g7)
    c: Coincident(g3,g5)
    c: Coincident(g8,g5)
    c: Tangent(g3,g8)
    c: Coincident(g7,g2)
    c: Coincident(g5,g-1)
    c: DistanceY(g0) = -3.3
    c: DistanceX(g0,g2) = 6.65
    c: Radius(g7) = 2.9
    c: Radius(g9) = 6.7
    c: PointOnObject(g9,g-1)
    c: PointOnObject(g9,g4)
    c: DistanceX(g6,g9) = 8.8
FEATURE [Sketcher::SketchObject] Sketch015  label="servo-top-1-sketch2"
  FullyConstrained = false
  MapMode = 5
  Placement = pos=(0,0,1.16) rot=(0,0,1;0rad)
  sketch-geometry (10):
    g0: LineSegment StartX=-8.99374 StartY=1.3 StartZ=0 EndX=-8.99374 EndY=-1.3 EndZ=0
    g1: ArcOfCircle CenterX=-8.99374 CenterY=0 CenterZ=0 NormalX=0 NormalY=0 NormalZ=1 AngleXU=0 Radius=1.3 StartAngle=1.5708 EndAngle=4.71239
    g2: LineSegment StartX=-8.99374 StartY=1.3 StartZ=0 EndX=-2.19374 EndY=1.3 EndZ=0
    g3: LineSegment StartX=-8.99374 StartY=-1.3 StartZ=0 EndX=-2.19374 EndY=-1.3 EndZ=0
    g4: LineSegment StartX=11.1937 StartY=1.3 StartZ=0 EndX=11.1937 EndY=-1.3 EndZ=0
    g5: ArcOfCircle CenterX=0 CenterY=0 CenterZ=0 NormalX=0 NormalY=0 NormalZ=1 AngleXU=0 Radius=2.55 StartAngle=3.67655 EndAngle=5.74823
    g6: LineSegment StartX=2.19374 StartY=1.3 StartZ=0 EndX=11.1937 EndY=1.3 EndZ=0
    g7: ArcOfCircle CenterX=0 CenterY=0 CenterZ=0 NormalX=0 NormalY=0 NormalZ=1 AngleXU=0 Radius=2.55 StartAngle=0.534957 EndAngle=2.60664
    g8: LineSegment StartX=2.19374 StartY=-1.3 StartZ=0 EndX=11.1937 EndY=-1.3 EndZ=0
    g9: Circle CenterX=11.1937 CenterY=0 CenterZ=0 NormalX=0 NormalY=0 NormalZ=1 AngleXU=0 Radius=6.7
  constraints (29):
    c: Vertical(g0)
    c: Symmetric(g0,g0,g-1)
    c: Coincident(g1,g0)
    c: Coincident(g0,g1)
    c: PointOnObject(g1,g0)
    c: Horizontal(g2)
    c: Coincident(g2,g0)
    c: Horizontal(g3)
    c: Coincident(g3,g0)
    c: Coincident(g6,g4)
    c: Vertical(g4)
    c: Coincident(g4,g8)
    c: Tangent(g2,g6)
    c: PointOnObject(g7,g2)
    c: Equal(g5,g7)
    c: Coincident(g7,g6)
    c: Coincident(g5,g7)
    c: Coincident(g3,g5)
    c: Coincident(g8,g5)
    c: Tangent(g3,g8)
    c: Coincident(g7,g2)
    c: Coincident(g5,g-1)
    c: DistanceY(g0) = -2.6
    c: DistanceX(g0,g2) = 6.8
    c: Radius(g7) = 2.55
    c: Radius(g9) = 6.7
    c: PointOnObject(g9,g-1)
    c: PointOnObject(g9,g4)
    c: DistanceX(g6,g9) = 9
FEATURE [Part::Loft] Loft  label="servo-top-1"
  Closed = false
  MaxDegree = 5
  Ruled = false
  Sections = -> [Sketch014,Sketch015]
  Solid = true
FEATURE [Sketcher::SketchObject] Sketch016  label="shaft-base-1-sketch"
  FullyConstrained = false
  MapMode = 5
  sketch-geometry (1):
    g0: Circle CenterX=0 CenterY=0 CenterZ=0 NormalX=0 NormalY=0 NormalZ=1 AngleXU=0 Radius=6.7
  constraints (2):
    c: Radius(g0) = 6.7
    c: Coincident(g-1,g0)
FEATURE [Sketcher::SketchObject] Sketch017  label="shaft-base-1-sketch2"
  FullyConstrained = false
  MapMode = 5
  Placement = pos=(0,0,2.2) rot=(0,0,1;0rad)
  sketch-geometry (1):
    g0: Circle CenterX=0 CenterY=0 CenterZ=0 NormalX=0 NormalY=0 NormalZ=1 AngleXU=0 Radius=5.85
  constraints (2):
    c: Radius(g0) = 5.85
    c: Coincident(g-1,g0)
FEATURE [Part::Loft] Loft001  label="Shaft-base-1"
  Closed = false
  MaxDegree = 5
  Placement = pos=(11.1848,0,0) rot=(0,0,1;0rad)
  Ruled = false
  Sections = -> [Sketch016,Sketch017]
  Solid = true
FEATURE [Part::MultiFuse] Fusion002  label="top-part-1"
  Shapes = -> [Loft,Loft001]
FEATURE [PartDesign::Fillet] Fillet
  Base = -> Fusion002 [Edge25]
  Radius = 0.5
  SupportTransform = false
FEATURE [Part::Fillet] Fillet001  label="top-part-2"
  Base = -> Fillet
  Edges = 8 edges r=0.1: [Edge6,Edge17,Edge19,Edge20,Edge21,Edge22,Edge23,Edge24]
FEATURE [App::DocumentObjectGroup] Group001  label="top-part-src"
  Group = -> [Fusion002,Fillet001]
FEATURE [Part::Feature] Fillet002  label="top-part"
  Placement = pos=(-0.634848,0,39.7) rot=(0,0,1;0rad)
  shape: bbox 28.82 x 13.4 x 14.16 mm, 24 faces (baked)
FEATURE [Sketcher::SketchObject] Sketch019  label="ears-body-1-sketch"
  FullyConstrained = false
  MapMode = 5
  sketch-geometry (4):
    g0: LineSegment StartX=-28 StartY=9.6 StartZ=0 EndX=28 EndY=9.6 EndZ=0
    g1: LineSegment StartX=28 StartY=9.6 StartZ=0 EndX=28 EndY=-9.6 EndZ=0
    g2: LineSegment StartX=28 StartY=-9.6 StartZ=0 EndX=-28 EndY=-9.6 EndZ=0
    g3: LineSegment StartX=-28 StartY=-9.6 StartZ=0 EndX=-28 EndY=9.6 EndZ=0
  constraints (11):
    c: Coincident(g0,g1)
    c: Coincident(g1,g2)
    c: Coincident(g2,g3)
    c: Coincident(g3,g0)
    c: Horizontal(g0)
    c: Horizontal(g2)
    c: Vertical(g1)
    c: Vertical(g3)
    c: Symmetric(g0,g1,g-1)
    c: DistanceX(g0) = 56
    c: DistanceY(g3) = 19.2
FEATURE [PartDesign::Pad] Pad002001003004001002  label="ears-body-1"
  AllowMultiFace = false
  Direction = (1,1,1)
  Length = 2.5
  Length2 = 100
  Profile = -> Sketch019
  Type = 0
FEATURE [Sketcher::SketchObject] Sketch020  label="right-ears-sketch"
  FullyConstrained = false
  MapMode = 5
  Placement = pos=(0,0,2.5) rot=(0,0,1;0rad)
  Support = -> [Pad002001003004001002]
  sketch-geometry (9):
    g0: ArcOfCircle CenterX=25.15 CenterY=5.1 CenterZ=0 NormalX=0 NormalY=0 NormalZ=1 AngleXU=0 Radius=2.25 StartAngle=0.605154 EndAngle=5.67803
    g1: LineSegment StartX=22.9 StartY=5.1 StartZ=0 EndX=25.15 EndY=5.1 EndZ=0
    g2: LineSegment StartX=27.0004 StartY=6.38 StartZ=0 EndX=29.0004 EndY=6.38 EndZ=0
    g3: LineSegment StartX=29.0004 StartY=6.38 StartZ=0 EndX=29.0004 EndY=3.82 EndZ=0
    g4: LineSegment StartX=29.0004 StartY=3.82 StartZ=0 EndX=27.0004 EndY=3.82 EndZ=0
    g5: ArcOfCircle CenterX=25.15 CenterY=-5.1 CenterZ=0 NormalX=0 NormalY=0 NormalZ=1 AngleXU=0 Radius=2.25 StartAngle=0.605154 EndAngle=5.67803
    g6: LineSegment StartX=27.0004 StartY=-3.82 StartZ=0 EndX=29.0004 EndY=-3.82 EndZ=0
    g7: LineSegment StartX=29.0004 StartY=-3.82 StartZ=0 EndX=29.0004 EndY=-6.38 EndZ=0
    g8: LineSegment StartX=29.0004 StartY=-6.38 StartZ=0 EndX=27.0004 EndY=-6.38 EndZ=0
  constraints (28):
    c: Radius(g0) = 2.25
    c: DistanceX(g0) = 25.15
    c: DistanceY(g0) = 5.1
    c: Horizontal(g1)
    c: PointOnObject(g1,g0)
    c: Coincident(g1,g0)
    c: Coincident(g2,g3)
    c: Coincident(g3,g4)
    c: Horizontal(g2)
    c: Horizontal(g4)
    c: Vertical(g3)
    c: Coincident(g0,g2)
    c: Coincident(g0,g4)
    c: Symmetric(g0,g0,g1)
    c: DistanceY(g3) = -2.56
    c: DistanceX(g2) = 2
    c: Symmetric(g5,g0,g-1)
    c: Equal(g0,g5)
    c: Coincident(g6,g7)
    c: Coincident(g7,g8)
    c: Horizontal(g6)
    c: Horizontal(g8)
    c: Vertical(g7)
    c: Coincident(g6,g5)
    c: Coincident(g8,g5)
    c: Symmetric(g5,g0,g-1)
    c: Symmetric(g0,g5,g-1)
    c: Symmetric(g6,g3,g-1)
FEATURE [PartDesign::Pocket] Pocket008  label="right-ear"
  AllowMultiFace = false
  Length = 5
  Length2 = 100
  Profile = -> Sketch020
  Type = 1
FEATURE [PartDesign::Mirrored] Mirrored001  label="ears-block-1"
  MirrorPlane = -> Sketch020 [V_Axis]
  Originals = -> [Pocket008]
FEATURE [Sketcher::SketchObject] Sketch021  label="ears-block-2-sketch"
  FullyConstrained = false
  MapMode = 5
  Placement = pos=(0,0,2.5) rot=(0,0,1;0rad)
  Support = -> [Mirrored001]
  sketch-geometry (6):
    g0: ArcOfCircle CenterX=-23.8 CenterY=0 CenterZ=0 NormalX=0 NormalY=0 NormalZ=1 AngleXU=0 Radius=1 StartAngle=1.57079 EndAngle=4.7124
    g1: ArcOfCircle CenterX=23.8 CenterY=0 CenterZ=0 NormalX=0 NormalY=0 NormalZ=1 AngleXU=0 Radius=1 StartAngle=4.71238 EndAngle=7.85399
    g2: LineSegment StartX=-23.8 StartY=-1 StartZ=0 EndX=23.8 EndY=-1 EndZ=0
    g3: LineSegment StartX=-23.8 StartY=1 StartZ=0 EndX=23.8 EndY=1 EndZ=0
    g4: GeomPoint X=-24.8 Y=0 Z=0
    g5: GeomPoint X=24.8 Y=0 Z=0
  constraints (18):
    c: Tangent(g0,g2)
    c: Tangent(g0,g3)
    c: Tangent(g1,g2)
    c: Tangent(g1,g3)
    c: Coincident(g0,g3)
    c: Coincident(g0,g2)
    c: Coincident(g2,g1)
    c: Coincident(g3,g1)
    c: Horizontal(g2)
    c: Equal(g0,g1)
    c: Symmetric(g0,g1,g-2)
    c: PointOnObject(g0,g-1)
    c: DistanceY(g0,g0) = 2
    c: PointOnObject(g4,g-1)
    c: PointOnObject(g4,g0)
    c: PointOnObject(g5,g-1)
    c: PointOnObject(g5,g1)
    c: DistanceX(g4,g5) = 49.6
FEATURE [PartDesign::Pad] Pad002001003004001003  label="ears-block-2"
  AllowMultiFace = false
  Direction = (1,1,1)
  Length = 0.86
  Length2 = 100
  Profile = -> Sketch021
  Type = 0
FEATURE [Sketcher::SketchObject] Sketch022  label="wire-holder-base-sketch"
  FullyConstrained = false
  MapMode = 5
  Placement = pos=(0,0,0) rot=(0.57735,0.57735,0.57735;2.0944rad)
  sketch-geometry (4):
    g0: LineSegment StartX=-3.4 StartY=2.15 StartZ=0 EndX=3.4 EndY=2.15 EndZ=0
    g1: LineSegment StartX=3.4 StartY=2.15 StartZ=0 EndX=3.4 EndY=-2.15 EndZ=0
    g2: LineSegment StartX=3.4 StartY=-2.15 StartZ=0 EndX=-3.4 EndY=-2.15 EndZ=0
    g3: LineSegment StartX=-3.4 StartY=-2.15 StartZ=0 EndX=-3.4 EndY=2.15 EndZ=0
  constraints (11):
    c: Coincident(g0,g1)
    c: Coincident(g1,g2)
    c: Coincident(g2,g3)
    c: Coincident(g3,g0)
    c: Horizontal(g0)
    c: Horizontal(g2)
    c: Vertical(g1)
    c: Vertical(g3)
    c: Symmetric(g0,g1,g-1)
    c: DistanceY(g1) = -4.3
    c: DistanceX(g0) = 6.8
FEATURE [PartDesign::Pad] Pad002001003004001005  label="wire-holder-base"
  AllowMultiFace = false
  Direction = (1,1,1)
  Length = 1.5
  Length2 = 100
  Placement = pos=(0,0,0) rot=(0.57735,0.57735,0.57735;2.0944rad)
  Profile = -> Sketch022
  Type = 0
FEATURE [Sketcher::SketchObject] Sketch023  label="wire-holder-body-1-sketch"
  FullyConstrained = false
  MapMode = 5
  Placement = pos=(0,0,0) rot=(0.57735,0.57735,0.57735;2.0944rad)
  sketch-geometry (4):
    g0: LineSegment StartX=-2.975 StartY=1.85 StartZ=0 EndX=2.975 EndY=1.85 EndZ=0
    g1: LineSegment StartX=2.975 StartY=1.85 StartZ=0 EndX=2.975 EndY=-1.85 EndZ=0
    g2: LineSegment StartX=2.975 StartY=-1.85 StartZ=0 EndX=-2.975 EndY=-1.85 EndZ=0
    g3: LineSegment StartX=-2.975 StartY=-1.85 StartZ=0 EndX=-2.975 EndY=1.85 EndZ=0
  constraints (11):
    c: Coincident(g0,g1)
    c: Coincident(g1,g2)
    c: Coincident(g2,g3)
    c: Coincident(g3,g0)
    c: Horizontal(g0)
    c: Horizontal(g2)
    c: Vertical(g1)
    c: Vertical(g3)
    c: Symmetric(g0,g1,g-1)
    c: DistanceX(g0) = 5.95
    c: DistanceY(g3) = 3.7
FEATURE [Sketcher::SketchObject] Sketch024  label="wire-holder-body-1-sketch2"
  FullyConstrained = false
  MapMode = 5
  Placement = pos=(4.2,0,0) rot=(0.57735,0.57735,0.57735;2.0944rad)
  sketch-geometry (4):
    g0: LineSegment StartX=-2.7 StartY=1.55 StartZ=0 EndX=2.7 EndY=1.55 EndZ=0
    g1: LineSegment StartX=2.7 StartY=1.55 StartZ=0 EndX=2.7 EndY=-1.55 EndZ=0
    g2: LineSegment StartX=2.7 StartY=-1.55 StartZ=0 EndX=-2.7 EndY=-1.55 EndZ=0
    g3: LineSegment StartX=-2.7 StartY=-1.55 StartZ=0 EndX=-2.7 EndY=1.55 EndZ=0
  constraints (11):
    c: Coincident(g0,g1)
    c: Coincident(g1,g2)
    c: Coincident(g2,g3)
    c: Coincident(g3,g0)
    c: Horizontal(g0)
    c: Horizontal(g2)
    c: Vertical(g1)
    c: Vertical(g3)
    c: Symmetric(g0,g1,g-1)
    c: DistanceX(g0) = 5.4
    c: DistanceY(g1) = -3.1
FEATURE [Part::Loft] Loft002  label="wire-holder-body-1"
  Closed = false
  MaxDegree = 5
  Ruled = false
  Sections = -> [Sketch023,Sketch024]
  Solid = true
FEATURE [Sketcher::SketchObject] Sketch025  label="wire-holes-sketch"
  FullyConstrained = false
  MapMode = 5
  Placement = pos=(4.2,-7e-16,0) rot=(0.57735,0.57735,0.57735;2.0944rad)
  Support = -> [Loft002]
  sketch-geometry (8):
    g0: ArcOfCircle CenterX=-1.2 CenterY=0 CenterZ=0 NormalX=0 NormalY=0 NormalZ=1 AngleXU=0 Radius=0.7 StartAngle=0.666946 EndAngle=5.61624
    g1: LineSegment StartX=-0.65 StartY=0.433013 StartZ=0 EndX=-0.55 EndY=0.433013 EndZ=0
    g2: ArcOfCircle CenterX=0 CenterY=0 CenterZ=0 NormalX=0 NormalY=0 NormalZ=1 AngleXU=0 Radius=0.7 StartAngle=0.666946 EndAngle=2.47465
    g3: LineSegment StartX=0.55 StartY=0.433013 StartZ=0 EndX=0.65 EndY=0.433013 EndZ=0
    g4: LineSegment StartX=-0.65 StartY=-0.433013 StartZ=0 EndX=-0.55 EndY=-0.433013 EndZ=0
    g5: ArcOfCircle CenterX=0 CenterY=0 CenterZ=0 NormalX=0 NormalY=0 NormalZ=1 AngleXU=0 Radius=0.7 StartAngle=3.80854 EndAngle=5.61624
    g6: ArcOfCircle CenterX=1.2 CenterY=0 CenterZ=0 NormalX=0 NormalY=0 NormalZ=1 AngleXU=0 Radius=0.7 StartAngle=3.80854 EndAngle=8.75783
    g7: LineSegment StartX=0.55 StartY=-0.433013 StartZ=0 EndX=0.65 EndY=-0.433013 EndZ=0
  constraints (26):
    c: PointOnObject(g0,g-1)
    c: Horizontal(g1)
    c: Coincident(g1,g0)
    c: Coincident(g3,g6)
    c: Coincident(g1,g2)
    c: Coincident(g3,g2)
    c: Tangent(g1,g3)
    c: Horizontal(g4)
    c: Symmetric(g0,g4,g-1)
    c: PointOnObject(g0,g4)
    c: PointOnObject(g6,g4)
    c: Coincident(g4,g5)
    c: Coincident(g7,g5)
    c: Tangent(g4,g7)
    c: PointOnObject(g7,g6)
    c: Equal(g1,g4)
    c: Equal(g4,g3)
    c: Equal(g3,g7)
    c: Equal(g5,g0)
    c: Equal(g0,g2)
    c: Equal(g2,g6)
    c: Radius(g6) = 0.7
    c: DistanceX(g0,g6) = 2.4
    c: Coincident(g5,g-1)
    c: Coincident(g2,g-1)
    c: DistanceX(g1) = 0.1
FEATURE [PartDesign::Pocket] Pocket009  label="wire-holder-body-2"
  AllowMultiFace = false
  Length = 5
  Length2 = 100
  Profile = -> Sketch025
  Type = 1
FEATURE [Part::Feature] Pocket010  label="wire-holder-body-2-copy"
  Placement = pos=(1.5,0,0) rot=(0,0,1;0rad)
  shape: bbox 4.2 x 5.95 x 3.7 mm, 14 faces (baked)
FEATURE [Part::MultiFuse] Fusion003  label="wire-holder-body-3"
  Shapes = -> [Pad002001003004001005,Pocket010]
FEATURE [Part::Fillet] Fillet003  label="wire-holder-body-4"
  Base = -> Fusion003
  Edges = 8 edges r=0.5: [Edge1,Edge2,Edge5,Edge8,Edge17,Edge18,Edge20,Edge22]
FEATURE [App::DocumentObjectGroup] Group003  label="wire-holder-src"
  Group = -> [Pad002001003004001005,Loft002,Pocket009,Pocket010,Fusion003,Fillet003]
FEATURE [Part::Feature] Fillet003001  label="wire-holder"
  Placement = pos=(20.55,0,6.35) rot=(0,0,1;0rad)
  shape: bbox 5.992 x 6.8 x 4.3 mm, 28 faces (baked)
FEATURE [Part::Fillet] Fillet003002
  Base = -> Pad002001003004001003
  Edges = 4 edges r=0.8: [Edge33,Edge34,Edge69,Edge71]
FEATURE [Part::Fillet] Fillet003003
  Base = -> Fillet003002
  Edges = 16 edges r=0.6: [Edge37,Edge39,Edge41,Edge43,Edge44,Edge46,Edge49,Edge51,Edge53,Edge55,Edge57,Edge59,Edge60,Edge62,Edge65,Edge67]
FEATURE [Part::Fillet] Fillet003004  label="ears-block-3"
  Base = -> Fillet003003
  Edges = 1 edges r=0.2: [Edge36]
FEATURE [Part::Fillet] Fillet003005  label="ears-block-4"
  Base = -> Fillet003004
  Edges = 1 edges r=0.2: [Edge132]
FEATURE [App::DocumentObjectGroup] Group002  label="ears-src"
  Group = -> [Pad002001003004001002,Pocket008,Mirrored001,Pad002001003004001003,Fillet003004,Fillet003005]
FEATURE [Part::Feature] Fillet003005001  label="ears"
  Placement = pos=(0,0,28.9) rot=(0,0,1;0rad)
  shape: bbox 56.13 x 19.33 x 3.36 mm, 91 faces (baked)
FEATURE [Sketcher::SketchObject] Sketch026  label="shaft-body-sketch"
  FullyConstrained = false
  MapMode = 5
  sketch-geometry (1):
    g0: Circle CenterX=0 CenterY=0 CenterZ=0 NormalX=0 NormalY=0 NormalZ=1 AngleXU=0 Radius=3
  constraints (2):
    c: Coincident(g0,g-1)
    c: Radius(g0) = 3
FEATURE [PartDesign::Pad] Pad002001003004001006  label="shaft-body"
  AllowMultiFace = false
  Direction = (1,1,1)
  Length = 4.4
  Length2 = 100
  Profile = -> Sketch026
  Type = 0
FEATURE [Sketcher::SketchObject] Sketch027  label="shaft-body-2-sketch"
  FullyConstrained = false
  MapMode = 5
  Placement = pos=(0,0,4.4) rot=(0,0,1;0rad)
  Support = -> [Pad002001003004001006]
  sketch-geometry (1):
    g0: Circle CenterX=0 CenterY=0 CenterZ=0 NormalX=0 NormalY=0 NormalZ=1 AngleXU=0 Radius=1.1
  constraints (2):
    c: Coincident(g0,g-1)
    c: Radius(g0) = 1.1
FEATURE [PartDesign::Pocket] Pocket011  label="shaft-body-2"
  AllowMultiFace = false
  Length = 5
  Length2 = 100
  Profile = -> Sketch027
  Type = 1
FEATURE [PartDesign::Chamfer] Chamfer  label="shaft-body-3"
  Angle = 45
  Base = -> Pocket011 [Edge3]
  ChamferType = 0
  FlipDirection = false
  Size = 0.3
  Size2 = 1
  SupportTransform = false
FEATURE [Sketcher::SketchObject] Sketch028  label="shaft-tooth-sketch"
  FullyConstrained = false
  MapMode = 5
  Placement = pos=(0,0,4.4) rot=(0,0,1;0rad)
  Support = -> [Chamfer]
  sketch-geometry (3):
    g0: LineSegment StartX=-0.2 StartY=3 StartZ=0 EndX=0 EndY=2.8 EndZ=0
    g1: LineSegment StartX=0.2 StartY=3 StartZ=0 EndX=0 EndY=2.8 EndZ=0
    g2: LineSegment StartX=-0.2 StartY=3 StartZ=0 EndX=0.2 EndY=3 EndZ=0
  constraints (8):
    c: Horizontal(g2)
    c: Coincident(g2,g0)
    c: Coincident(g2,g1)
    c: Symmetric(g0,g1,g-2)
    c: DistanceX(g2) = 0.4
    c: Coincident(g0,g1)
    c: PointOnObject(g0,g-2)
    c: DistanceY(g0,g1) = 0.2
FEATURE [PartDesign::Pocket] Pocket012  label="shaft-tooth"
  AllowMultiFace = false
  Length = 3.4
  Length2 = 100
  Profile = -> Sketch028
  Type = 0
FEATURE [PartDesign::PolarPattern] PolarPattern  label="shaft-teeth"
  Angle = 360
  Axis = -> Sketch028 [N_Axis]
  Occurrences = 28
  Originals = -> [Pocket012]
FEATURE [PartDesign::Chamfer] Chamfer001  label="shaft-final"
  Angle = 45
  Base = -> PolarPattern [Edge286]
  ChamferType = 0
  FlipDirection = false
  Size = 0.3
  Size2 = 1
  SupportTransform = false
FEATURE [App::DocumentObjectGroup] Group004  label="shaft-src"
  Group = -> [Pad002001003004001006,Pocket011,Chamfer,Pocket012,PolarPattern,Chamfer001]
FEATURE [Part::Feature] Chamfer001001  label="shaft"
  Placement = pos=(10.55,0,41.9) rot=(0,0,1;0rad)
  shape: bbox 6 x 6 x 4.4 mm, 90 faces (baked)
FEATURE [Part::Feature] Pad002001003004001007  label="bottom-side-gap"
  Placement = pos=(0,0,7.5) rot=(0,0,1;0rad)
  shape: bbox 44.1 x 24.8 x 0.4 mm, 14 faces (baked)
FEATURE [Part::Feature] Pad002001003004001007001  label="top-side-gap"
  Placement = pos=(0,0,28.5) rot=(0,0,1;0rad)
  shape: bbox 44.1 x 24.8 x 0.4 mm, 14 faces (baked)
FEATURE [Part::MultiFuse] Fusion004  label="side-gaps"
  Shapes = -> [Pad002001003004001007,Pad002001003004001007001]
FEATURE [PartDesign::Fillet] Fillet003005005  label="servo-body-final-3"
  Base = -> Pad002001003003 [Edge31,Edge38,Edge25,Edge32]
  Radius = 2
  SupportTransform = false
FEATURE [Part::Cut] Cut001002002  label="servo-body-final-4"
  Base = -> Fillet003005005
  Tool = -> Fusion004
FEATURE [Part::Fillet] Fillet003005006  label="servo-body-final-5"
  Base = -> Cut001002002
  Edges = 3 edges r=0.3: [Edge1,Edge3,Edge14]
FEATURE [App::DocumentObjectGroup] Group  label="Servo-body-src"
  Group = -> [Pad,Pocket,Mirrored,Pocket001,Pocket002,Pocket003,Pocket004,Pocket005,Pocket006,Pad001,Pad002,Cut,Pad002001003003,Pad002001003004,Pad002001003004001007,Pad002001003004001007001,Fusion004,Fillet003005005,Cut001002002,Fillet003005006]
FEATURE [Part::Feature] Fillet003005006001  label="servo-body"
  shape: bbox 41.26 x 21.13 x 39.7 mm, 208 faces (baked)
FEATURE [Part::MultiFuse] Fusion005  label="servo-1"
  Shapes = -> [Fillet002,Fillet003005001,Fillet003001,Fillet003005006001]
FEATURE [Part::Feature] Cut001002003  label="bottom-screw-1"
  Placement = pos=(-18.1075,7.95754,34.2) rot=(1,0,0;3.14159rad)
  shape: bbox 3.75 x 3.75 x 33.19 mm, 18 faces (baked)
FEATURE [Part::Feature] Cut001002004  label="bottom-screw-2"
  Placement = pos=(18.1075,-7.95754,34.2) rot=(1,0,0;3.14159rad)
  shape: bbox 3.75 x 3.75 x 33.19 mm, 18 faces (baked)
FEATURE [Part::Feature] Cut001002005  label="bottom-screw-3"
  Placement = pos=(18.1075,7.95754,34.2) rot=(1,0,0;3.14159rad)
  shape: bbox 3.75 x 3.75 x 33.19 mm, 18 faces (baked)
FEATURE [Part::Feature] Cut001002006  label="bottom-screw-4"
  Placement = pos=(-18.1075,-7.95754,34.2) rot=(1,0,0;3.14159rad)
  shape: bbox 3.75 x 3.75 x 33.19 mm, 18 faces (baked)
FEATURE [Part::Compound] Compound  label="bottom-screws"
  Links = -> [Cut001002003,Cut001002006,Cut001002004,Cut001002005]
FEATURE [Part::Cylinder] Cylinder  label="wire-center"
  Angle = 360
  AttacherType = Attacher::AttachEngine3D
  Height = 10
  Placement = pos=(1.5,0,0) rot=(0,1,0;1.5708rad)
  Radius = 0.65
FEATURE [Part::Feature] Cylinder001  label="wire-right"
  Placement = pos=(1.5,1.2,-8e-16) rot=(0,1,0;1.5708rad)
  shape: bbox 10 x 1.3 x 1.3 mm, 3 faces (baked)
FEATURE [Part::Feature] Cylinder002  label="wire-left"
  Placement = pos=(1.5,-1.2,3e-16) rot=(0,1,0;1.5708rad)
  shape: bbox 10 x 1.3 x 1.3 mm, 3 faces (baked)
FEATURE [Part::MultiFuse] Fusion006  label="wires"
  Placement = pos=(20.55,0,6.35) rot=(0,0,1;0rad)
  Shapes = -> [Cylinder,Cylinder001,Cylinder002]
FEATURE [Part::Compound] Compound001  label="Servo-SM-S4303R-assembly"
  Links = -> [Chamfer001001,Fusion005,Fusion006,Compound]
FEATURE [Part::Feature] Chamfer001002  label="shaft001"
  Placement = pos=(10.55,0,41.9) rot=(0,0,1;0rad)
  shape: bbox 6 x 6 x 4.4 mm, 90 faces (baked)
FEATURE [Part::Feature] Fusion007  label="wires001"
  Placement = pos=(20.55,0,6.35) rot=(0,0,1;0rad)
  shape: bbox 10 x 3.7 x 1.3 mm, 9 faces (baked)
FEATURE [Part::Feature] Fusion008  label="servo-002"
  shape: bbox 56.13 x 21.13 x 45.15 mm, 371 faces (baked)
FEATURE [Part::Feature] Compound003  label="bottom-screws001"
  shape: bbox 39.97 x 19.67 x 33.19 mm, 72 faces, 4 solids (baked)
FEATURE [Part::Compound] Compound002  label="Servo-SM-S4303R-compound"
  Links = -> [Compound003,Fusion008,Fusion007,Chamfer001002]
FEATURE [Part::Compound] Compound004  label="Servo-SM-S4303R"
